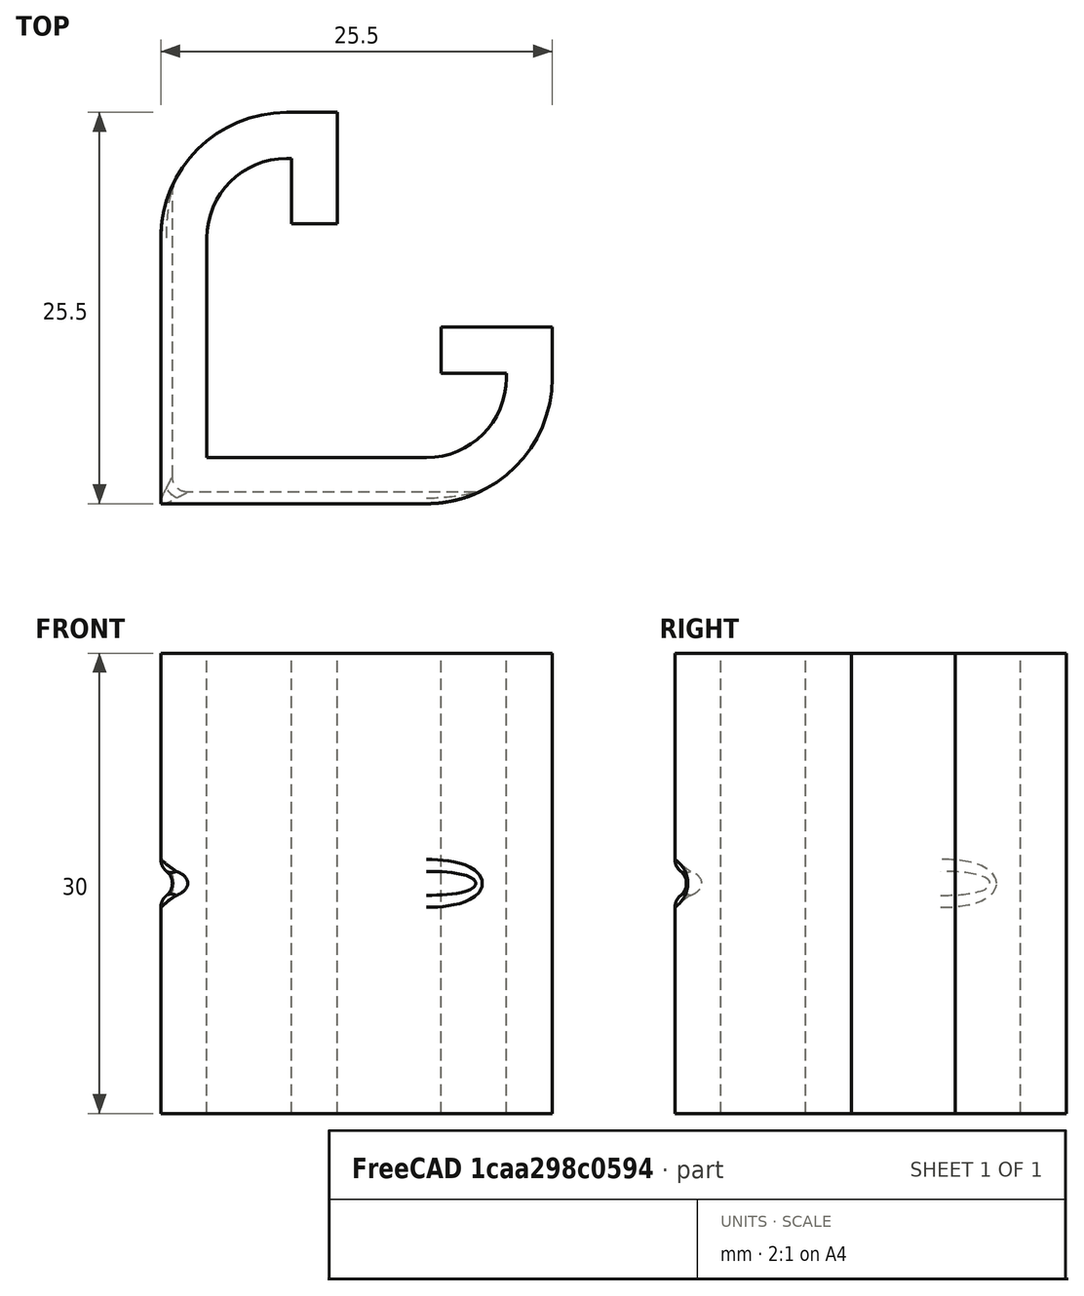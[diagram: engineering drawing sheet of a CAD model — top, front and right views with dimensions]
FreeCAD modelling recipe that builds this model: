
FCSTD DOCUMENT  (FreeCAD 0.17R13541 (Git))
Label: ListeSamler
License: All rights reserved
LicenseURL: http://en.wikipedia.org/wiki/All_rights_reserved
objects: Sketcher::SketchObject×4, PartDesign::Pad×2, PartDesign::Body×2, App::Part×2, PartDesign::Pocket×2, Spreadsheet::Sheet×1, PartDesign::Fillet×1, PartDesign::FeatureBase×1, Mesh::Feature×1
note: 16 computed .brp shape members not serialized (recipe doc carries the construction recipe); baked Part::Feature solids carry a one-line shape summary decoded from their .brp

FEATURE [Sketcher::SketchObject] Sketch
  MapMode = 5
  Support = -> [XY_Plane]
  expr: Constraints[4] = D.ListeBredde
  expr: Constraints[12] = D.ListeDybde
  expr: Constraints[5] = D.ListeBredde
  expr: Constraints[2] = D.ListeDybde
  sketch-geometry (6):
    g0: LineSegment StartX=-1e-12 StartY=14 StartZ=0 EndX=0 EndY=0 EndZ=0
    g1: LineSegment StartX=-5 StartY=-5 StartZ=0 EndX=-5 EndY=9 EndZ=0
    g2: ArcOfCircle CenterX=0 CenterY=9 CenterZ=0 NormalX=0 NormalY=0 NormalZ=1 AngleXU=0 Radius=5 StartAngle=1.5708 EndAngle=3.14159
    g3: LineSegment StartX=-5 StartY=-5 StartZ=0 EndX=9 EndY=-5 EndZ=0
    g4: LineSegment StartX=0 StartY=2e-12 StartZ=0 EndX=14 EndY=2e-12 EndZ=0
    g5: ArcOfCircle CenterX=9 CenterY=0 CenterZ=0 NormalX=0 NormalY=0 NormalZ=1 AngleXU=0 Radius=5 StartAngle=4.71239 EndAngle=6.28319
  constraints (17):
    c: PointOnObject(g0,g-2)
    c: Coincident(g0,g-1)
    c: Distance(g0) = 14
    c: Vertical(g1)
    c: DistanceX(g1,g-1) = 5
    c: DistanceY(g1,g-1) = 5
    c: Tangent(g1,g2) = 1.5708
    c: PointOnObject(g2,g0)
    c: Coincident(g3,g1)
    c: Horizontal(g3)
    c: Coincident(g4,g-1)
    c: Horizontal(g4)
    c: Distance(g4) = 14
    c: Tangent(g3,g5) = -1.5708
    c: PointOnObject(g5,g4)
    c: Coincident(g5,g4)
    c: Coincident(g2,g0)
FEATURE [PartDesign::Pad] Pad
  Length = 100
  Length2 = 100
  Midplane = true
  Profile = -> Sketch
  Type = 0
FEATURE [PartDesign::Body] Body  label="Liste"
  Group = -> [Sketch,Pad]
  Origin = -> Origin
  Tip = -> Pad
FEATURE [Sketcher::SketchObject] Sketch001
  MapMode = 5
  Support = -> [XY_Plane001]
  expr: Constraints[45] = D.SamTyk
  expr: Constraints[33] = D.CentAfs
  expr: Constraints.FiletOffset = D.Offset * 1.25
  expr: Constraints[46] = D.Offset * 1.25
  expr: Constraints[40] = D.SamTyk
  expr: Constraints[31] = D.ListeBredde + D.Offset
  expr: Constraints[25] = D.ListeBredde + D.Offset
  expr: Constraints[28] = D.SamTyk
  expr: Constraints[30] = D.Offset
  expr: Constraints[29] = D.ListeDybde + D.Offset
  expr: Constraints[32] = D.CentAfs
  expr: Constraints[24] = D.Offset + D.ListeDybde
  expr: Constraints[27] = D.SamTyk
  expr: Constraints[39] = D.SamTyk
  expr: Constraints[44] = D.SamTyk
  expr: Constraints[23] = D.Offset
  sketch-geometry (18):
    g0: LineSegment StartX=-8.25 StartY=-8.25 StartZ=0 EndX=-8.25 EndY=9.0625 EndZ=0
    g1: LineSegment StartX=-0.0625 StartY=17.25 StartZ=0 EndX=3.25 EndY=17.25 EndZ=0
    g2: LineSegment StartX=3.25 StartY=17.25 StartZ=0 EndX=3.25 EndY=10 EndZ=0
    g3: LineSegment StartX=3.25 StartY=10 StartZ=0 EndX=0.25 EndY=10 EndZ=0
    g4: LineSegment StartX=0.25 StartY=10 StartZ=0 EndX=0.25 EndY=14.25 EndZ=0
    g5: LineSegment StartX=-8.25 StartY=-8.25 StartZ=0 EndX=9.0625 EndY=-8.25 EndZ=0
    g6: LineSegment StartX=17.25 StartY=-0.0625 StartZ=0 EndX=17.25 EndY=3.25 EndZ=0
    g7: LineSegment StartX=17.25 StartY=3.25 StartZ=0 EndX=10 EndY=3.25 EndZ=0
    g8: LineSegment StartX=10 StartY=3.25 StartZ=0 EndX=10 EndY=0.25 EndZ=0
    g9: LineSegment StartX=10 StartY=0.25 StartZ=0 EndX=14.25 EndY=0.25 EndZ=0
    g10: LineSegment StartX=14.25 StartY=0.25 StartZ=0 EndX=14.25 EndY=-0.0625 EndZ=0
    g11: LineSegment StartX=-5.25 StartY=-5.25 StartZ=0 EndX=-5.25 EndY=9.0625 EndZ=0
    g12: LineSegment StartX=9.0625 StartY=-5.25 StartZ=0 EndX=-5.25 EndY=-5.25 EndZ=0
    g13: LineSegment StartX=-0.0625 StartY=14.25 StartZ=0 EndX=0.25 EndY=14.25 EndZ=0
    g14: ArcOfCircle CenterX=-0.0625 CenterY=9.0625 CenterZ=0 NormalX=0 NormalY=0 NormalZ=1 AngleXU=0 Radius=5.1875 StartAngle=1.5708 EndAngle=3.14159
    g15: ArcOfCircle CenterX=-0.0625 CenterY=9.0625 CenterZ=0 NormalX=0 NormalY=0 NormalZ=1 AngleXU=0 Radius=8.1875 StartAngle=1.5708 EndAngle=3.14159
    g16: ArcOfCircle CenterX=9.0625 CenterY=-0.0625 CenterZ=0 NormalX=0 NormalY=0 NormalZ=1 AngleXU=0 Radius=5.1875 StartAngle=4.71239 EndAngle=6.28319
    g17: ArcOfCircle CenterX=9.0625 CenterY=-0.0625 CenterZ=0 NormalX=0 NormalY=0 NormalZ=1 AngleXU=0 Radius=8.1875 StartAngle=4.71239 EndAngle=6.28319
  constraints (50):
    c: Vertical(g0)
    c: Horizontal(g1)
    c: Coincident(g2,g1)
    c: Vertical(g2)
    c: Coincident(g3,g2)
    c: Horizontal(g3)
    c: Coincident(g4,g3)
    c: Coincident(g5,g0)
    c: Horizontal(g5)
    c: Vertical(g6)
    c: Coincident(g7,g6)
    c: Horizontal(g7)
    c: Coincident(g8,g7)
    c: Vertical(g8)
    c: Coincident(g9,g8)
    c: Horizontal(g9)
    c: Coincident(g10,g9)
    c: Vertical(g10)
    c: Vertical(g11)
    c: Coincident(g12,g11)
    c: Coincident(g13,g4)
    c: Horizontal(g13)
    c: Vertical(g4)
    c: DistanceX(g-1,g3) = 0.25
    c: DistanceY(g-1,g4) = 14.25
    c: Distance(g-1,g11) = 5.25
    c: Horizontal(g12)
    c: DistanceX(g4,g1) = 3
    c: DistanceY(g9,g6) = 3
    c: DistanceX(g-1,g9) = 14.25
    c: DistanceY(g-1,g8) = 0.25
    c: DistanceY(g11,g-1) = 5.25
    c: DistanceX(g-1,g8) = 10
    c: DistanceY(g-1,g3) = 10
    c: Tangent(g11,g14) = 1.5708
    c: Tangent(g13,g14) = 1.5708
    c: DistanceX(g13,g4) = 0.3125  'FiletOffset'
    c: Tangent(g0,g15) = 1.5708
    c: Tangent(g1,g15) = 1.5708
    c: DistanceY(g4,g1) = 3
    c: DistanceX(g0,g11) = 3
    c: Vertical(g13,g1)
    c: Tangent(g10,g16) = 1.5708
    c: Tangent(g12,g16) = 1.5708
    c: DistanceY(g0,g11) = 3
    c: DistanceX(g9,g6) = 3
    c: DistanceY(g10,g9) = 0.3125
    c: Tangent(g5,g17) = -1.5708
    c: Tangent(g6,g17) = -1.5708
    c: Horizontal(g6,g10)
FEATURE [Spreadsheet::Sheet] Spreadsheet  label="D"
  cells = B2=Data; B3=Offset; C3(Offset)==0.25mm; B4=ListeBredde; C4(ListeBredde)==5mm; B5=ListeDybde; C5(ListeDybde)==14mm; B6=SamlingTykkelse; C6(SamTyk)==3mm; B7=CenterAfstand; C7(CentAfs)==10mm; B8=CutOutRadius; C8(CutRad)==1mm
FEATURE [PartDesign::Pad] Pad001
  Length = 30
  Length2 = 100
  Midplane = true
  Profile = -> Sketch001
  Type = 0
FEATURE [App::Part] Part001  label="TestListe"
  Group = -> [Body]
  License = CC BY 3.0
  LicenseURL = http://creativecommons.org/licenses/by/3.0/
  Origin = -> Origin003
  Placement = pos=(0,0,-51) rot=(0,0,1;0rad)
FEATURE [Sketcher::SketchObject] Sketch002
  MapMode = 5
  Placement = pos=(0,-8.25,0) rot=(1,0,0;1.5708rad)
  Support = -> [Pad001]
  expr: Constraints[2] = D.CutRad
  expr: Constraints[1] = D.CutRad * 0.25 + D.ListeBredde + D.Offset + D.SamTyk
  sketch-geometry (1):
    g0: Circle CenterX=-8.5 CenterY=0 CenterZ=0 NormalX=0 NormalY=0 NormalZ=1 AngleXU=0 Radius=1
  constraints (3):
    c: PointOnObject(g0,g-1)
    c: Distance(g-1,g0) = 8.5
    c: Radius(g0) = 1
FEATURE [PartDesign::Pocket] Pocket
  BaseFeature = -> Pad001
  Length = 5
  Length2 = 100
  Profile = -> Sketch002
  Type = 1
FEATURE [Sketcher::SketchObject] Sketch003
  MapMode = 5
  Placement = pos=(-8.25,0,0) rot=(0.57735,-0.57735,-0.57735;2.0944rad)
  Support = -> [Pocket]
  expr: Constraints[2] = D.CutRad
  expr: Constraints[1] = D.CutRad * 0.25 + D.ListeBredde + D.Offset + D.SamTyk
  sketch-geometry (1):
    g0: Circle CenterX=8.5 CenterY=0 CenterZ=0 NormalX=0 NormalY=0 NormalZ=1 AngleXU=0 Radius=1
  constraints (3):
    c: PointOnObject(g0,g-1)
    c: DistanceX(g-1,g0) = 8.5
    c: Radius(g0) = 1
FEATURE [PartDesign::Pocket] Pocket001
  BaseFeature = -> Pocket
  Length = 5
  Length2 = 100
  Profile = -> Sketch003
  Type = 1
FEATURE [PartDesign::Fillet] Fillet
  Base = -> Pocket001 [Face4,Face24]
  BaseFeature = -> Pocket001
  Radius = 1
FEATURE [PartDesign::Body] Body001  label="Samler"
  Group = -> [Sketch001,Pad001,Sketch002,Pocket,Sketch003,Pocket001,Fillet]
  Origin = -> Origin001
  Tip = -> Fillet
FEATURE [App::Part] Part  label="ListeSamler"
  Group = -> [Body001]
  License = CC BY 3.0
  LicenseURL = http://creativecommons.org/licenses/by/3.0/
  Origin = -> Origin002
FEATURE [PartDesign::FeatureBase] Clone
  BaseFeature = -> Body
  Placement = pos=(0,0,51) rot=(0,0,1;0rad)
FEATURE [Mesh::Feature] Mesh  label="Samler (Meshed)"
